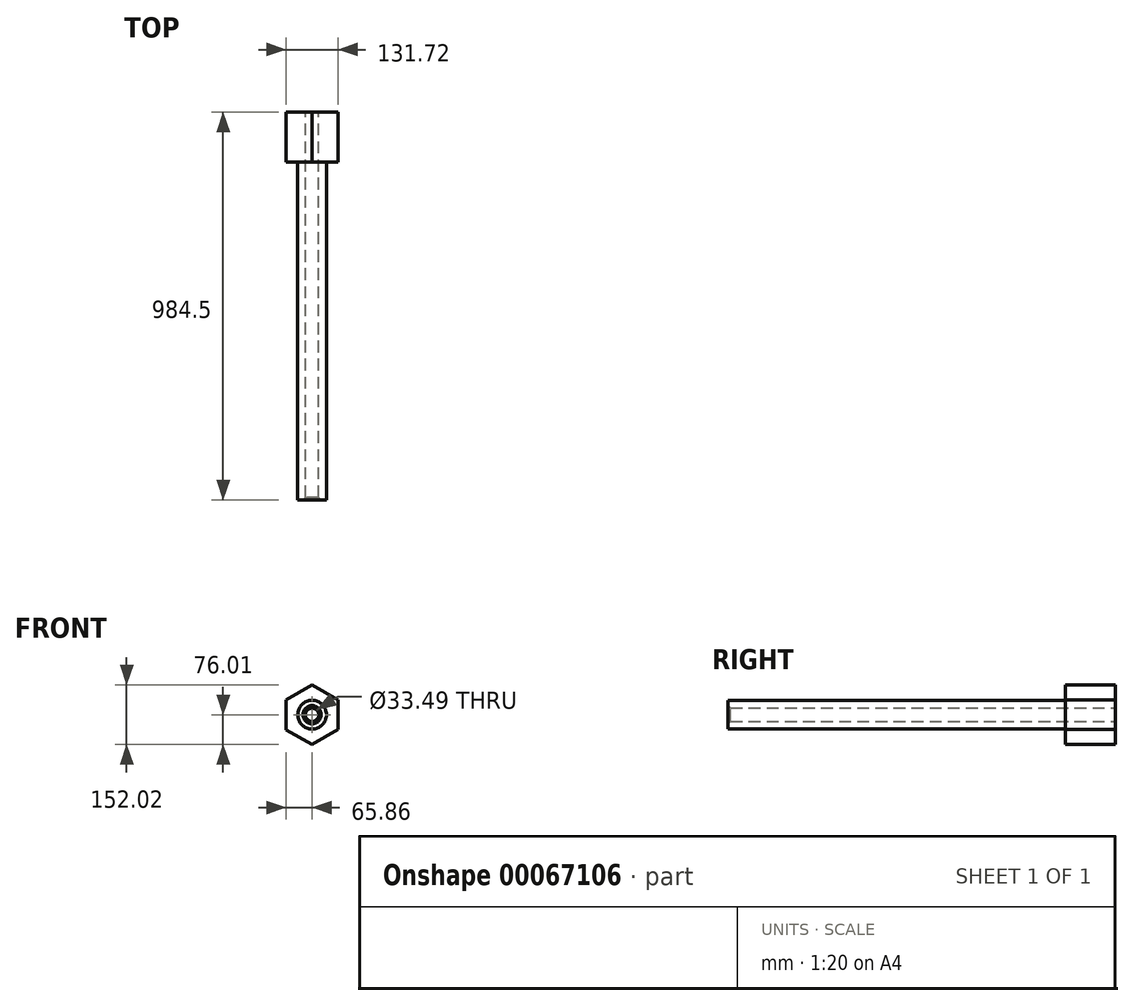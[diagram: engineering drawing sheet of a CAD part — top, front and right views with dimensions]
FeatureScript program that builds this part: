
annotation { "Feature Type Name" : "Feature", "Feature Type Description" : "" }
export const myFeature = defineFeature(function(context is Context, id is Id, definition is map)
    precondition{}
    {
        {
            var Q0;
            Q0=qCreatedBy(makeId("Front.planeOp"),FACE);
            var sketch = newSketch(context, id + "F0", { "sketchPlane" : qUnion([Q0])});
            skCircle(sketch, "E0.cCircle", {"center": v(0, 0) * mm, "radius": 65.83 * mm, "construction": true});
            skLineSegment(sketch, "E0.0", {"start": v(65.86, -37.95) * mm, "end": v(0.07, -76.01) * mm});
            skLineSegment(sketch, "E0.1", {"start": v(0.07, -76.01) * mm, "end": v(-65.8, -38.07) * mm});
            skLineSegment(sketch, "E0.2", {"start": v(-65.8, -38.07) * mm, "end": v(-65.86, 37.95) * mm});
            skLineSegment(sketch, "E0.3", {"start": v(-65.86, 37.95) * mm, "end": v(-0.07, 76.01) * mm});
            skLineSegment(sketch, "E0.4", {"start": v(-0.07, 76.01) * mm, "end": v(65.8, 38.07) * mm});
            skLineSegment(sketch, "E0.5", {"start": v(65.8, 38.07) * mm, "end": v(65.86, -37.95) * mm});
            skPoint(sketch, "E0.0.midPoint", {"position": v(32.97, -56.98) * mm});
            skCircle(sketch, "E1", {"center": v(0, 0) * mm, "radius": 36.43 * mm});
            skCircle(sketch, "E2", {"center": v(0, 0) * mm, "radius": 16.75 * mm});
            skSolve(sketch);
        }
        {
            var Q0;
            Q0=makeQuery(id+"F0.imprint","IMPRINT",FACE,{"disambiguationData":[TD([[makeQuery(id+"F0.imprint","IMPRINT",EDGE,{"derivedFrom":sQuery(id+"F0.wireOp",EDGE,"E1")}),1.0]])]});
            extrude(context, id + "F1", {"entities" : qUnion([Q0]), "depth" : 984.5 * mm});
        }
        {
            var Q0;
            Q0=makeQuery(id+"F0.imprint","IMPRINT",FACE,{"disambiguationData":[TD([[makeQuery(id+"F0.imprint","IMPRINT",EDGE,{"derivedFrom":sQuery(id+"F0.wireOp",EDGE,"E0.0")}),-1.0]])]});
            extrude(context, id + "F2", {"entities" : qUnion([Q0]), "operationType" : NewBodyOperationType.ADD, "depth" : 127 * mm});
        }
        {
            var Q0;
            Q0=qCreatedBy(makeId("Front.planeOp"),FACE);
            var sketch = newSketch(context, id + "F3", { "sketchPlane" : qUnion([Q0])});
            skCircle(sketch, "E3", {"center": v(0, 0) * mm, "radius": 28.05 * mm});
            skSolve(sketch);
        }
        {
            var Q0;
            Q0=sQuery(id+"F3.wireOp",EDGE,"E3");
            extrude(context, id + "F4", {"bodyType" : ToolBodyType.SURFACE, "surfaceEntities" : qUnion([Q0]), "oppositeDirection" : true, "depth" : 1697.07 * mm});
        }
        {
            var Q0;
            Q0=makeQuery(id+"F1.opExtrude","CAP_EDGE",EDGE,{"disambiguationData":[OSD([sQuery(id+"F0.wireOp",EDGE,"E2")])],"isStart":false});
            chamfer(context, id + "F5", {"entities" : qUnion([Q0]), "width" : 6.35 * mm, "tangentPropagation" : true});
        }
    });
